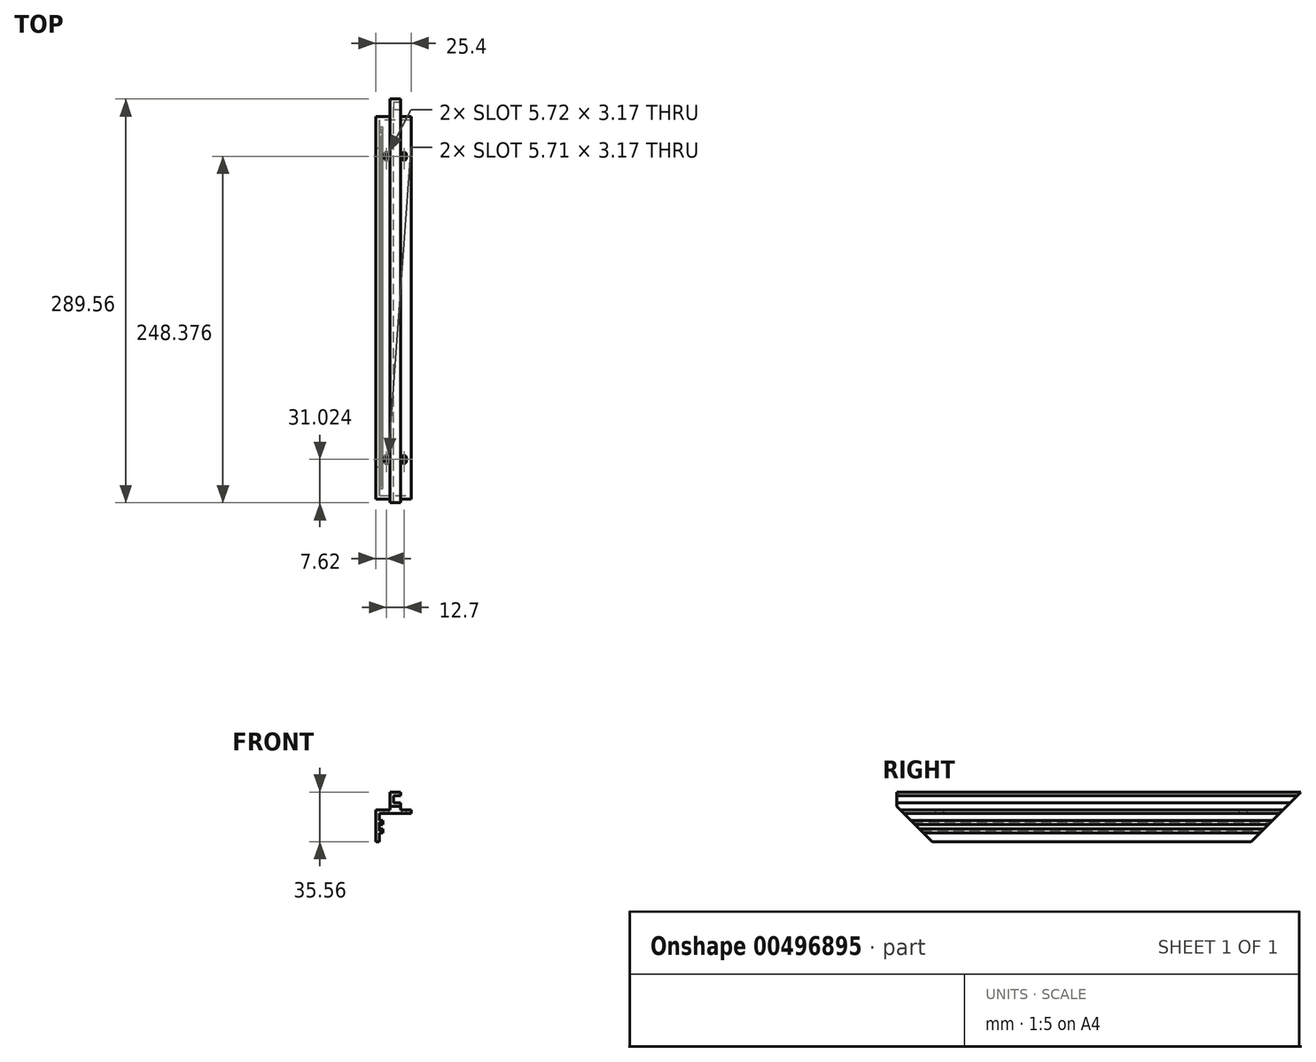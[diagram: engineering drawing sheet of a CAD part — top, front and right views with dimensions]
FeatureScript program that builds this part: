
annotation { "Feature Type Name" : "Feature", "Feature Type Description" : "" }
export const myFeature = defineFeature(function(context is Context, id is Id, definition is map)
    precondition{}
    {
        {
            var Q0;
            Q0=qCreatedBy(makeId("Front.planeOp"),FACE);
            var sketch = newSketch(context, id + "F0", { "sketchPlane" : qUnion([Q0])});
            skLineSegment(sketch, "E0", {"start": v(0, 0) * mm, "end": v(2.54, 0) * mm});
            skLineSegment(sketch, "E1", {"start": v(2.54, 0) * mm, "end": v(2.54, 6.35) * mm});
            skLineSegment(sketch, "E2", {"start": v(2.54, 20.32) * mm, "end": v(25.4, 20.32) * mm});
            skLineSegment(sketch, "E3", {"start": v(25.4, 20.32) * mm, "end": v(25.4, 22.86) * mm});
            skLineSegment(sketch, "E4", {"start": v(25.4, 22.86) * mm, "end": v(17.78, 22.86) * mm});
            skLineSegment(sketch, "E5", {"start": v(10.16, 22.86) * mm, "end": v(0, 22.86) * mm});
            skLineSegment(sketch, "E6", {"start": v(0, 22.86) * mm, "end": v(0, 0) * mm});
            skLineSegment(sketch, "E7", {"start": v(17.78, 22.86) * mm, "end": v(17.78, 27.94) * mm});
            skLineSegment(sketch, "E8", {"start": v(17.78, 27.94) * mm, "end": v(12.7, 27.94) * mm});
            skLineSegment(sketch, "E9", {"start": v(12.7, 27.94) * mm, "end": v(12.7, 33.02) * mm});
            skLineSegment(sketch, "E10", {"start": v(12.7, 33.02) * mm, "end": v(17.78, 33.02) * mm});
            skLineSegment(sketch, "E11", {"start": v(17.78, 33.02) * mm, "end": v(17.78, 35.56) * mm});
            skLineSegment(sketch, "E12", {"start": v(17.78, 35.56) * mm, "end": v(10.16, 35.56) * mm});
            skLineSegment(sketch, "E13", {"start": v(10.16, 35.56) * mm, "end": v(10.16, 22.86) * mm});
            skLineSegment(sketch, "E14", {"start": v(2.54, 15.24) * mm, "end": v(5.08, 15.24) * mm});
            skLineSegment(sketch, "E15", {"start": v(5.08, 15.24) * mm, "end": v(5.08, 12.45) * mm});
            skLineSegment(sketch, "E16", {"start": v(5.08, 6.35) * mm, "end": v(2.54, 6.35) * mm});
            skLineSegment(sketch, "E17.trimOffspring", {"start": v(2.54, 15.24) * mm, "end": v(2.54, 20.32) * mm});
            skLineSegment(sketch, "E18.bottom", {"start": v(2.54, 13.97) * mm, "end": v(3.81, 13.97) * mm});
            skLineSegment(sketch, "E18.top", {"start": v(2.54, 7.62) * mm, "end": v(3.81, 7.62) * mm});
            skLineSegment(sketch, "E18.left", {"start": v(2.54, 13.97) * mm, "end": v(2.54, 7.62) * mm});
            skLineSegment(sketch, "E18.right", {"start": v(3.81, 13.97) * mm, "end": v(3.81, 12.45) * mm});
            skLineSegment(sketch, "E19.bottom", {"start": v(3.81, 12.45) * mm, "end": v(5.08, 12.45) * mm});
            skLineSegment(sketch, "E19.top", {"start": v(3.81, 9.14) * mm, "end": v(5.08, 9.14) * mm});
            skLineSegment(sketch, "E20.trimOffspring", {"start": v(5.08, 9.14) * mm, "end": v(5.08, 6.35) * mm});
            skLineSegment(sketch, "E21.trimOffspring", {"start": v(3.81, 9.14) * mm, "end": v(3.81, 7.62) * mm});
            skSolve(sketch);
        }
        {
            var Q0;
            Q0=qSketchRegion(id+"F0",true);
            extrude(context, id + "F1", {"entities" : qUnion([Q0]), "depth" : 304.8 * mm});
        }
        {
            var Q0;
            Q0=makeQuery(id+"F1.opExtrude","SWEPT_FACE",FACE,{"disambiguationData":[OSD([sQuery(id+"F0.wireOp",EDGE,"E6")])]});
            var sketch = newSketch(context, id + "F2", { "sketchPlane" : qUnion([Q0])});
            skLineSegment(sketch, "E22", {"start": v(0, 0) * mm, "end": v(0, 38.1) * mm});
            skLineSegment(sketch, "E23", {"start": v(0, 38.1) * mm, "end": v(38.1, 0) * mm});
            skLineSegment(sketch, "E24", {"start": v(38.1, 0) * mm, "end": v(0, 0) * mm});
            skLineSegment(sketch, "E25", {"start": v(304.8, 38.1) * mm, "end": v(304.8, 0) * mm});
            skLineSegment(sketch, "E26", {"start": v(304.8, 0) * mm, "end": v(266.7, 0) * mm});
            skLineSegment(sketch, "E27", {"start": v(266.7, 0) * mm, "end": v(304.8, 38.1) * mm});
            skSolve(sketch);
        }
        {
            var Q0;
            Q0=qSketchRegion(id+"F2",true);
            extrude(context, id + "F3", {"entities" : qUnion([Q0]), "operationType" : NewBodyOperationType.REMOVE, "oppositeDirection" : true, "depth" : 25.4 * mm});
        }
        {
            var Q0;
            Q0=makeQuery(id+"F1.opExtrude","SWEPT_FACE",FACE,{"disambiguationData":[OSD([sQuery(id+"F0.wireOp",EDGE,"E1")])]});
            var sketch = newSketch(context, id + "F4", { "sketchPlane" : qUnion([Q0])});
            skLineSegment(sketch, "E28", {"start": v(-292.1, 35.56) * mm, "end": v(-302.26, 35.56) * mm});
            skLineSegment(sketch, "E29", {"start": v(-302.26, 35.56) * mm, "end": v(-292.1, 25.4) * mm});
            skLineSegment(sketch, "E30", {"start": v(-292.1, 35.56) * mm, "end": v(-292.1, 25.4) * mm});
            skSolve(sketch);
        }
        {
            var Q0;
            Q0 = qSketchRegion(id + "F4", true);
            extrude(context, id + "F5", {"entities" : qUnion([Q0]), "operationType" : NewBodyOperationType.REMOVE, "endBound" : BoundingType.SYMMETRIC, "oppositeDirection" : true, "depth" : 101.6 * mm});
        }
        {
            var Q0;
            Q0=makeQuery(id+"F1.opExtrude","SWEPT_FACE",FACE,{"disambiguationData":[OSD([sQuery(id+"F0.wireOp",EDGE,"E5")])]});
            var sketch = newSketch(context, id + "F6", { "sketchPlane" : qUnion([Q0])});
            skLineSegment(sketch, "E31", {"start": v(6.03, -259.8) * mm, "end": v(6.03, -262.35) * mm});
            skLineSegment(sketch, "E32", {"start": v(9.2, -262.35) * mm, "end": v(9.2, -259.8) * mm});
            skArc(sketch, "E33", {"start": v(6.03, -259.8) * mm, "mid": v(7.62, -258.22) * mm, "end": v(9.2, -259.8) * mm});
            skArc(sketch, "E34", {"start": v(9.2, -262.35) * mm, "mid": v(7.62, -263.93) * mm, "end": v(6.03, -262.35) * mm});
            skLineSegment(sketch, "E35", {"start": v(7.62, -287.02) * mm, "end": v(7.62, -243.38) * mm, "construction": true});
            skLineSegment(sketch, "E36", {"start": v(13.97, -292.1) * mm, "end": v(13.97, -246.15) * mm, "construction": true});
            skLineSegment(sketch, "E37.MirrorCS", {"start": v(21.9, -259.8) * mm, "end": v(21.9, -262.35) * mm});
            skLineSegment(sketch, "E38.MirrorCS", {"start": v(18.73, -262.35) * mm, "end": v(18.73, -259.8) * mm});
            skArc(sketch, "E39.MirrorCS", {"start": v(21.9, -259.8) * mm, "mid": v(20.32, -258.22) * mm, "end": v(18.73, -259.8) * mm});
            skArc(sketch, "E40.MirrorCS", {"start": v(18.73, -262.35) * mm, "mid": v(20.32, -263.93) * mm, "end": v(21.9, -262.35) * mm});
            skLineSegment(sketch, "E41.MirrorCS", {"start": v(20.32, -287.02) * mm, "end": v(20.32, -243.38) * mm, "construction": true});
            skLineSegment(sketch, "E42", {"start": v(0, -152.4) * mm, "end": v(32.73, -152.4) * mm, "construction": true});
            skPoint(sketch, "E42.endSnap0", {"position": v(0, -152.4) * mm});
            skLineSegment(sketch, "E43.MirrorCS", {"start": v(9.2, -42.45) * mm, "end": v(9.2, -45) * mm});
            skArc(sketch, "E44.MirrorCS", {"start": v(9.2, -42.45) * mm, "mid": v(7.62, -40.87) * mm, "end": v(6.03, -42.45) * mm});
            skArc(sketch, "E45.MirrorCS", {"start": v(6.03, -45) * mm, "mid": v(7.62, -46.58) * mm, "end": v(9.2, -45) * mm});
            skLineSegment(sketch, "E46.MirrorCS", {"start": v(6.03, -45) * mm, "end": v(6.03, -42.45) * mm});
            skLineSegment(sketch, "E47.MirrorCS", {"start": v(18.73, -42.45) * mm, "end": v(18.73, -45) * mm});
            skLineSegment(sketch, "E48.MirrorCS", {"start": v(21.9, -45) * mm, "end": v(21.9, -42.45) * mm});
            skArc(sketch, "E49.MirrorCS", {"start": v(18.73, -42.45) * mm, "mid": v(20.32, -40.87) * mm, "end": v(21.9, -42.45) * mm});
            skArc(sketch, "E50.MirrorCS", {"start": v(21.9, -45) * mm, "mid": v(20.32, -46.58) * mm, "end": v(18.73, -45) * mm});
            skLineSegment(sketch, "E51.MirrorCS", {"start": v(13.97, -12.7) * mm, "end": v(13.97, -58.65) * mm, "construction": true});
            skLineSegment(sketch, "E52.MirrorCS", {"start": v(7.62, -17.78) * mm, "end": v(7.62, -61.42) * mm, "construction": true});
            skLineSegment(sketch, "E53.MirrorCS", {"start": v(20.32, -17.78) * mm, "end": v(20.32, -61.42) * mm, "construction": true});
            skSolve(sketch);
        }
        {
            var Q0;
            Q0 = qSketchRegion(id + "F6", true);
            extrude(context, id + "F7", {"entities" : qUnion([Q0]), "operationType" : NewBodyOperationType.REMOVE, "oppositeDirection" : true, "depth" : 25.4 * mm});
        }
    });
